# Revit family: DVNS
name_source: partatom
category: Wyposażenie mechaniczne
revit_build: Autodesk Revit 2017 (Build: 20160225_1515(x64)
units: mm (PartAtom-declared; Revit-internal decimal feet)

## family parameters
Oparty na płaszczyźnie roboczej = Nie
Punkt obliczania pomieszczeń = Nie
Tnij formami wycięć po wczytaniu = Nie
Typ części = Normalny
Współdzielony = Nie
Wymiar okrągłego złącza = Użyj średnicy
Zawsze pionowo = Tak

## types (27) — shared parameters
Air_flow = 0.0 m³/h
Date = 11.2018
Frequency = 50 Hz
Pressure = 0.0 Pa
Producent = Rosenberg
URL = https://www.rosenberg.pl
Version = 1
t1 = 2 mm  [stored 0.00656168 ft]

## per-type parameters (varying)
| type | A | Current | Da | Di | H | Height | Height_1 | Height_2 | L | P | Power | Protection_class | Voltage | Weight[kg] | Width | Width_bottom | max.Ambient_temperature |
| 310L-4 E | 395 mm  [stored 1.29593 ft] | 1 A | 306 mm  [stored 1.00394 ft] | 256 mm  [stored 0.839895 ft] | 700 mm  [stored 2.29659 ft] | 390 mm  [stored 1.27953 ft] | 450 mm  [stored 1.47638 ft] | 140 mm  [stored 0.459318 ft] | 156 mm  [stored 0.511811 ft] | 657 mm | 0 kW | IP54 | 230 V | 24.5 | 720 mm  [stored 2.3622 ft] | 435 mm  [stored 1.42717 ft] | 120 °C |
| 355-4 E | 555 mm  [stored 1.82087 ft] | 2 A | 464 mm  [stored 1.52231 ft] | 402 mm  [stored 1.3189 ft] | 900 mm  [stored 2.95276 ft] | 445 mm  [stored 1.45997 ft] | 550 mm | 185 mm | 220 mm  [stored 0.721785 ft] | 817 mm  [stored 2.68045 ft] | 0 kW | IP55 | 230 V | 120 | 915 mm  [stored 3.00197 ft] | 595 mm  [stored 1.9521 ft] | 120 °C |
| 400-4 E | 555 mm  [stored 1.82087 ft] | 2 A | 464 mm  [stored 1.52231 ft] | 402 mm  [stored 1.3189 ft] | 900 mm  [stored 2.95276 ft] | 445 mm  [stored 1.45997 ft] | 550 mm | 185 mm | 220 mm  [stored 0.721785 ft] | 817 mm  [stored 2.68045 ft] | 1 kW | IP55 | 230 V | 48 | 915 mm  [stored 3.00197 ft] | 595 mm  [stored 1.9521 ft] | 120 °C |
| 450-4 E | 625 mm  [stored 2.05052 ft] | 4 A | 464 mm  [stored 1.52231 ft] | 402 mm  [stored 1.3189 ft] | 900 mm  [stored 2.95276 ft] | 480 mm  [stored 1.5748 ft] | 550 mm | 150 mm  [stored 0.492126 ft] | 220 mm  [stored 0.721785 ft] | 877 mm  [stored 2.8773 ft] | 1 kW | IP54 | 230 V | 47 | 1005 mm  [stored 3.29724 ft] | 665 mm  [stored 2.18176 ft] | 120 °C |
| 310L-4 D | 395 mm  [stored 1.29593 ft] | 1 A | 306 mm  [stored 1.00394 ft] | 256 mm  [stored 0.839895 ft] | 700 mm  [stored 2.29659 ft] | 390 mm  [stored 1.27953 ft] | 450 mm  [stored 1.47638 ft] | 140 mm  [stored 0.459318 ft] | 156 mm  [stored 0.511811 ft] | 657 mm | 0 kW | IP54 | 400 V | 19 | 720 mm  [stored 2.3622 ft] | 435 mm  [stored 1.42717 ft] | 120 °C |
| 355-4 D | 555 mm  [stored 1.82087 ft] | 1 A | 464 mm  [stored 1.52231 ft] | 402 mm  [stored 1.3189 ft] | 900 mm  [stored 2.95276 ft] | 445 mm  [stored 1.45997 ft] | 550 mm | 185 mm | 220 mm  [stored 0.721785 ft] | 817 mm  [stored 2.68045 ft] | 0 kW | IP55 | 400 V | 40 | 915 mm  [stored 3.00197 ft] | 595 mm  [stored 1.9521 ft] | 120 °C |
| 400-4 D | 555 mm  [stored 1.82087 ft] | 1 A | 464 mm  [stored 1.52231 ft] | 402 mm  [stored 1.3189 ft] | 900 mm  [stored 2.95276 ft] | 445 mm  [stored 1.45997 ft] | 550 mm | 185 mm | 220 mm  [stored 0.721785 ft] | 817 mm  [stored 2.68045 ft] | 1 kW | IP55 | 400 V | 48 | 915 mm  [stored 3.00197 ft] | 595 mm  [stored 1.9521 ft] | 120 °C |
| 450-4 D | 555 mm  [stored 1.82087 ft] | 2 A | 464 mm  [stored 1.52231 ft] | 402 mm  [stored 1.3189 ft] | 900 mm  [stored 2.95276 ft] | 445 mm  [stored 1.45997 ft] | 550 mm | 185 mm | 220 mm  [stored 0.721785 ft] | 817 mm  [stored 2.68045 ft] | 1 kW | IP55 | 400 V | 60.5 | 915 mm  [stored 3.00197 ft] | 595 mm  [stored 1.9521 ft] | 120 °C |
| 500-4 D | 555 mm  [stored 1.82087 ft] | 3 A | 464 mm  [stored 1.52231 ft] | 402 mm  [stored 1.3189 ft] | 900 mm  [stored 2.95276 ft] | 480 mm  [stored 1.5748 ft] | 550 mm | 150 mm  [stored 0.492126 ft] | 220 mm  [stored 0.721785 ft] | 817 mm  [stored 2.68045 ft] | 2 kW | IP55 | 400 V | 67.5 | 1005 mm  [stored 3.29724 ft] | 665 mm  [stored 2.18176 ft] | 120 °C |
| 560-4 D | 555 mm  [stored 1.82087 ft] | 5 A | 464 mm  [stored 1.52231 ft] | 402 mm  [stored 1.3189 ft] | 900 mm  [stored 2.95276 ft] | 600 mm | 850 mm  [stored 2.78871 ft] | 330 mm  [stored 1.08268 ft] | 220 mm  [stored 0.721785 ft] | 817 mm  [stored 2.68045 ft] | 3 kW | IP55 | 400 V | 124 | 1405 mm  [stored 4.60958 ft] | 939 mm  [stored 3.08071 ft] | 120 °C |
| 630-4 D | 555 mm  [stored 1.82087 ft] | 11 A | 464 mm  [stored 1.52231 ft] | 402 mm  [stored 1.3189 ft] | 900 mm  [stored 2.95276 ft] | 600 mm | 850 mm  [stored 2.78871 ft] | 330 mm  [stored 1.08268 ft] | 220 mm  [stored 0.721785 ft] | 817 mm  [stored 2.68045 ft] | 6 kW | IP55 | 400 V | 113 | 1405 mm  [stored 4.60958 ft] | 939 mm  [stored 3.08071 ft] | 120 °C |
| 710-6 D | 555 mm  [stored 1.82087 ft] | 10 A | 464 mm  [stored 1.52231 ft] | 402 mm  [stored 1.3189 ft] | 900 mm  [stored 2.95276 ft] | 700 mm  [stored 2.29659 ft] | 950 mm  [stored 3.1168 ft] | 330 mm  [stored 1.08268 ft] | 220 mm  [stored 0.721785 ft] | 817 mm  [stored 2.68045 ft] | 3 kW | IP55 | 400 V | 160 | 1510 mm | 1035 mm  [stored 3.39567 ft] | 120 °C |
| 800-6 D | 555 mm  [stored 1.82087 ft] | 12 A | 464 mm  [stored 1.52231 ft] | 402 mm  [stored 1.3189 ft] | 900 mm  [stored 2.95276 ft] | 700 mm  [stored 2.29659 ft] | 950 mm  [stored 3.1168 ft] | 330 mm  [stored 1.08268 ft] | 220 mm  [stored 0.721785 ft] | 817 mm  [stored 2.68045 ft] | 5 kW | IP55 | 400 V | 200 | 1510 mm | 1035 mm  [stored 3.39567 ft] | 100 °C |
| 900-6 D | 555 mm  [stored 1.82087 ft] | 17 A | 464 mm  [stored 1.52231 ft] | 402 mm  [stored 1.3189 ft] | 900 mm  [stored 2.95276 ft] | 845 mm  [stored 2.77231 ft] | 1150 mm | 385 mm | 220 mm  [stored 0.721785 ft] | 817 mm  [stored 2.68045 ft] | 8 kW | IP54 | 400 V | 243 | 1815 mm | 1250 mm  [stored 4.10105 ft] | 100 °C |
| 900-8 D | 555 mm  [stored 1.82087 ft] | 8 A | 464 mm  [stored 1.52231 ft] | 402 mm  [stored 1.3189 ft] | 900 mm  [stored 2.95276 ft] | 845 mm  [stored 2.77231 ft] | 1150 mm | 385 mm | 220 mm  [stored 0.721785 ft] | 817 mm  [stored 2.68045 ft] | 3 kW | IP54 | 400 V | 275 | 1815 mm | 1250 mm  [stored 4.10105 ft] | 120 °C |
| 355-4D Exde | 555 mm  [stored 1.82087 ft] | 1 A | 464 mm  [stored 1.52231 ft] | 402 mm  [stored 1.3189 ft] | 900 mm  [stored 2.95276 ft] | 445 mm  [stored 1.45997 ft] | 550 mm | 185 mm | 220 mm  [stored 0.721785 ft] | 817 mm  [stored 2.68045 ft] | 1 kW | IP55 | 400 V | 62 | 915 mm  [stored 3.00197 ft] | 595 mm  [stored 1.9521 ft] | 40 °C |
| 355-4D Exe | 555 mm  [stored 1.82087 ft] | 2 A | 464 mm  [stored 1.52231 ft] | 402 mm  [stored 1.3189 ft] | 900 mm  [stored 2.95276 ft] | 445 mm  [stored 1.45997 ft] | 550 mm | 185 mm | 220 mm  [stored 0.721785 ft] | 817 mm  [stored 2.68045 ft] | 1 kW | IP55 | 400 V | 48 | 915 mm  [stored 3.00197 ft] | 595 mm  [stored 1.9521 ft] | 40 °C |
| 400-4D Exde | 555 mm  [stored 1.82087 ft] | 1 A | 464 mm  [stored 1.52231 ft] | 402 mm  [stored 1.3189 ft] | 900 mm  [stored 2.95276 ft] | 445 mm  [stored 1.45997 ft] | 550 mm | 185 mm | 220 mm  [stored 0.721785 ft] | 817 mm  [stored 2.68045 ft] | 1 kW | IP55 | 400 V | 62 | 915 mm  [stored 3.00197 ft] | 595 mm  [stored 1.9521 ft] | 40 °C |
| 400-4D Exe | 555 mm  [stored 1.82087 ft] | 2 A | 464 mm  [stored 1.52231 ft] | 402 mm  [stored 1.3189 ft] | 900 mm  [stored 2.95276 ft] | 445 mm  [stored 1.45997 ft] | 550 mm | 185 mm | 220 mm  [stored 0.721785 ft] | 817 mm  [stored 2.68045 ft] | 1 kW | IP55 | 400 V | 48 | 915 mm  [stored 3.00197 ft] | 595 mm  [stored 1.9521 ft] | 40 °C |
| 450-4D Exde | 555 mm  [stored 1.82087 ft] | 2 A | 464 mm  [stored 1.52231 ft] | 402 mm  [stored 1.3189 ft] | 900 mm  [stored 2.95276 ft] | 480 mm  [stored 1.5748 ft] | 550 mm | 150 mm  [stored 0.492126 ft] | 220 mm  [stored 0.721785 ft] | 817 mm  [stored 2.68045 ft] | 1 kW | IP55 | 400 V | 71 | 1005 mm  [stored 3.29724 ft] | 665 mm  [stored 2.18176 ft] | 40 °C |
| 450-4D Exe | 555 mm  [stored 1.82087 ft] | 2 A | 464 mm  [stored 1.52231 ft] | 402 mm  [stored 1.3189 ft] | 900 mm  [stored 2.95276 ft] | 480 mm  [stored 1.5748 ft] | 550 mm | 150 mm  [stored 0.492126 ft] | 220 mm  [stored 0.721785 ft] | 817 mm  [stored 2.68045 ft] | 1 kW | IP55 | 400 V | 56 | 1005 mm  [stored 3.29724 ft] | 665 mm  [stored 2.18176 ft] | 40 °C |
| 500-4D Exe | 555 mm  [stored 1.82087 ft] | 5 A | 464 mm  [stored 1.52231 ft] | 402 mm  [stored 1.3189 ft] | 900 mm  [stored 2.95276 ft] | 480 mm  [stored 1.5748 ft] | 550 mm | 150 mm  [stored 0.492126 ft] | 220 mm  [stored 0.721785 ft] | 817 mm  [stored 2.68045 ft] | 2 kW | IP55 | 400 V | 60 | 1005 mm  [stored 3.29724 ft] | 665 mm  [stored 2.18176 ft] | 40 °C |
| 500-4D Exde | 555 mm  [stored 1.82087 ft] | 5 A | 464 mm  [stored 1.52231 ft] | 402 mm  [stored 1.3189 ft] | 900 mm  [stored 2.95276 ft] | 480 mm  [stored 1.5748 ft] | 550 mm | 150 mm  [stored 0.492126 ft] | 220 mm  [stored 0.721785 ft] | 817 mm  [stored 2.68045 ft] | 2 kW | IP55 | 400 V | 60 | 1005 mm  [stored 3.29724 ft] | 665 mm  [stored 2.18176 ft] | 40 °C |
| 560-4D Exde | 555 mm  [stored 1.82087 ft] | 7 A | 464 mm  [stored 1.52231 ft] | 402 mm  [stored 1.3189 ft] | 900 mm  [stored 2.95276 ft] | 600 mm | 850 mm  [stored 2.78871 ft] | 330 mm  [stored 1.08268 ft] | 220 mm  [stored 0.721785 ft] | 817 mm  [stored 2.68045 ft] | 3 kW | IP55 | 400 V | 120 | 1405 mm  [stored 4.60958 ft] | 939 mm  [stored 3.08071 ft] | 40 °C |
| 560-4D Exe | 555 mm  [stored 1.82087 ft] | 8 A | 464 mm  [stored 1.52231 ft] | 402 mm  [stored 1.3189 ft] | 900 mm  [stored 2.95276 ft] | 600 mm | 850 mm  [stored 2.78871 ft] | 330 mm  [stored 1.08268 ft] | 220 mm  [stored 0.721785 ft] | 817 mm  [stored 2.68045 ft] | 4 kW | IP55 | 400 V | 113 | 1405 mm  [stored 4.60958 ft] | 939 mm  [stored 3.08071 ft] | 40 °C |
| 630-4D Exde | 555 mm  [stored 1.82087 ft] | 11 A | 464 mm  [stored 1.52231 ft] | 402 mm  [stored 1.3189 ft] | 900 mm  [stored 2.95276 ft] | 600 mm | 850 mm  [stored 2.78871 ft] | 330 mm  [stored 1.08268 ft] | 220 mm  [stored 0.721785 ft] | 817 mm  [stored 2.68045 ft] | 6 kW | IP55 | 400 V | 113 | 1405 mm  [stored 4.60958 ft] | 939 mm  [stored 3.08071 ft] | 40 °C |
| 630-4D Exe | 555 mm  [stored 1.82087 ft] | 10 A | 464 mm  [stored 1.52231 ft] | 402 mm  [stored 1.3189 ft] | 900 mm  [stored 2.95276 ft] | 600 mm | 850 mm  [stored 2.78871 ft] | 330 mm  [stored 1.08268 ft] | 220 mm  [stored 0.721785 ft] | 817 mm  [stored 2.68045 ft] | 5 kW | IP55 | 400 V | 113 | 1405 mm  [stored 4.60958 ft] | 939 mm  [stored 3.08071 ft] | 40 °C |

note: column(s) folded — value = type name in every type: Model

note: [stored X ft] marks values corroborated as IEEE doubles in the binary element streams (Revit-internal decimal feet)
